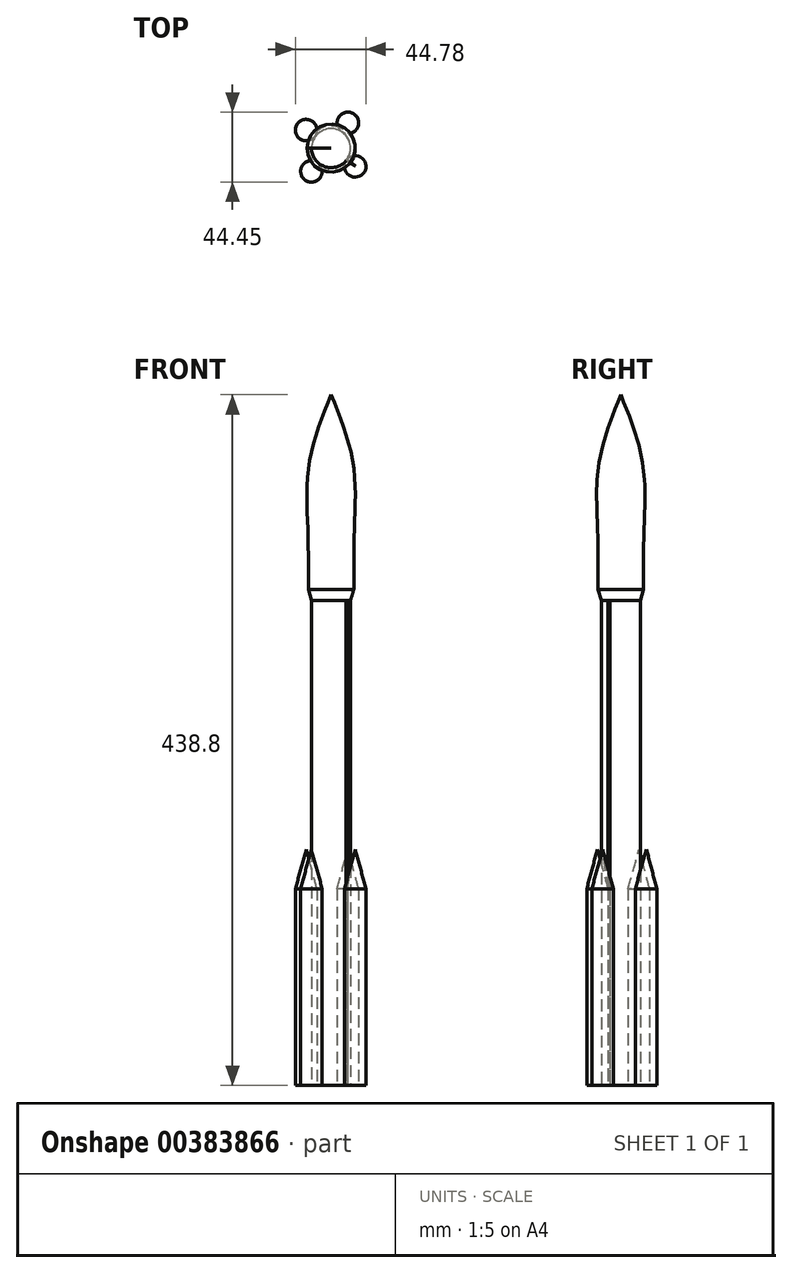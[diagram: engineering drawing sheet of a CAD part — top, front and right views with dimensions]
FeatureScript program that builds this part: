
annotation { "Feature Type Name" : "Feature", "Feature Type Description" : "" }
export const myFeature = defineFeature(function(context is Context, id is Id, definition is map)
    precondition{}
    {
        {
            var Q0;
            Q0=qCreatedBy(makeId("Top.planeOp"),FACE);
            var sketch = newSketch(context, id + "F0", { "sketchPlane" : qUnion([Q0])});
            skCircle(sketch, "E0", {"center": v(0, 0) * mm, "radius": 12.42 * mm});
            skCircle(sketch, "E1", {"center": v(-15.81, 11.43) * mm, "radius": 6.83 * mm});
            skCircle(sketch, "E2", {"center": v(10.7, 16.03) * mm, "radius": 6.83 * mm});
            skCircle(sketch, "E3", {"center": v(-12.48, -14.76) * mm, "radius": 6.83 * mm});
            skCircle(sketch, "E4", {"center": v(15.3, -11.59) * mm, "radius": 6.83 * mm});
            skSolve(sketch);
        }
        {
            var Q0;
            {var subQ0=sQuery(id+"F0.wireOp",EDGE,"E4");var subQ1=sQuery(id+"F0.wireOp",EDGE,"E0");var subQ2=makeQuery(id+"F0.imprint","INTERSECT",VERTEX,{"disambiguationData":[OD(0.0)],"derivedFrom":[subQ1,subQ0]});Q0=makeQuery(id+"F0.imprint","IMPRINT",FACE,{"disambiguationData":[TD([[makeQuery(id+"F0.imprint","IMPRINT",EDGE,{"disambiguationData":[TD([[subQ2,1.0]])],"derivedFrom":subQ1}),1.0]])]});}
            extrude(context, id + "F1", {"entities" : qUnion([Q0]), "depth" : 308 * mm});
        }
        {
            var Q0;
            {var subQ0=sQuery(id+"F0.wireOp",EDGE,"E4");var subQ1=sQuery(id+"F0.wireOp",EDGE,"E0");var subQ2=makeQuery(id+"F0.imprint","INTERSECT",VERTEX,{"disambiguationData":[OD(0.0)],"derivedFrom":[subQ1,subQ0]});Q0=makeQuery(id+"F0.imprint","IMPRINT",FACE,{"disambiguationData":[TD([[makeQuery(id+"F0.imprint","IMPRINT",EDGE,{"disambiguationData":[TD([[subQ2,-1.0]])],"derivedFrom":subQ1}),-1.0]])]});}
            var Q1;
            Q1=makeQuery(id+"F0.imprint","IMPRINT",FACE,{"disambiguationData":[TD([[makeQuery(id+"F0.imprint","IMPRINT",EDGE,{"derivedFrom":sQuery(id+"F0.wireOp",EDGE,"E2")}),1.0]])]});
            var Q2;
            Q2=makeQuery(id+"F0.imprint","IMPRINT",FACE,{"disambiguationData":[TD([[makeQuery(id+"F0.imprint","IMPRINT",EDGE,{"derivedFrom":sQuery(id+"F0.wireOp",EDGE,"E3")}),1.0]])]});
            var Q3;
            Q3=makeQuery(id+"F0.imprint","IMPRINT",FACE,{"disambiguationData":[TD([[makeQuery(id+"F0.imprint","IMPRINT",EDGE,{"derivedFrom":sQuery(id+"F0.wireOp",EDGE,"E1")}),1.0]])]});
            extrude(context, id + "F2", {"entities" : qUnion([Q0, Q1, Q2, Q3]), "depth" : 125 * mm});
        }
        {
            var Q0;
            Q0=makeQuery(id+"F2.opExtrude","CAP_FACE",FACE,{"disambiguationData":[OSD([sQuery(id+"F0.wireOp",EDGE,"E3")])],"isStart":false});
            cPlane(context, id + "F3", {"entities" : qUnion([Q0]), "cplaneType" : CPlaneType.OFFSET, "offset" : 25 * mm, "width" : 150 * mm, "height" : 150 * mm});
        }
        {
            var Q0;
            Q0=qCreatedBy(id+"F3.planeOp",FACE);
            var sketch = newSketch(context, id + "F4", { "sketchPlane" : qUnion([Q0])});
            skCircle(sketch, "E5", {"center": v(-15.72, 11.64) * mm, "radius": 0.7 * mm});
            skCircle(sketch, "E6", {"center": v(-12.58, -14.84) * mm, "radius": 0.65 * mm});
            skCircle(sketch, "E7", {"center": v(15.36, -11.48) * mm, "radius": 0.68 * mm});
            skCircle(sketch, "E8", {"center": v(10.65, 16.24) * mm, "radius": 0.68 * mm});
            skSolve(sketch);
        }
        {
            var Q0;
            Q0=makeQuery(id+"F2.opExtrude","CAP_FACE",FACE,{"disambiguationData":[OSD([sQuery(id+"F0.wireOp",EDGE,"E3")])],"isStart":false});
            var Q1;
            Q1=sQuery(id+"F4.wireOp",VERTEX,"E6.center");
            loft(context, id + "F5", {"sheetProfilesArray" : [{ "sheetProfileEntities" : qUnion([Q0]) }, { "sheetProfileEntities" : qUnion([Q1]) }]});
        }
        {
            var Q1;
            Q1=makeQuery(id+"F2.opExtrude","CAP_FACE",FACE,{"disambiguationData":[OSD([sQuery(id+"F0.wireOp",EDGE,"E0"),sQuery(id+"F0.wireOp",EDGE,"E4")])],"isStart":false});
            var Q2;
            Q2=sQuery(id+"F4.wireOp",VERTEX,"E7.center");
            loft(context, id + "F6", {"operationType" : NewBodyOperationType.ADD, "sheetProfilesArray" : [{ "sheetProfileEntities" : qUnion([Q1]) }, { "sheetProfileEntities" : qUnion([Q2]) }]});
        }
        {
            var Q0;
            Q0=makeQuery(id+"F2.opExtrude","CAP_FACE",FACE,{"disambiguationData":[OSD([sQuery(id+"F0.wireOp",EDGE,"E1")])],"isStart":false});
            var Q1;
            Q1=sQuery(id+"F4.wireOp",VERTEX,"E5.center");
            loft(context, id + "F7", {"sheetProfilesArray" : [{ "sheetProfileEntities" : qUnion([Q0]) }, { "sheetProfileEntities" : qUnion([Q1]) }]});
        }
        {
            var Q0;
            Q0=makeQuery(id+"F2.opExtrude","CAP_FACE",FACE,{"disambiguationData":[OSD([sQuery(id+"F0.wireOp",EDGE,"E2")])],"isStart":false});
            var Q1;
            Q1=sQuery(id+"F4.wireOp",VERTEX,"E8.center");
            loft(context, id + "F8", {"sheetProfilesArray" : [{ "sheetProfileEntities" : qUnion([Q0]) }, { "sheetProfileEntities" : qUnion([Q1]) }]});
        }
        {
            var Q0;
            Q0=makeQuery(id+"F1.opExtrude","CAP_FACE",FACE,{"disambiguationData":[OSD([sQuery(id+"F0.wireOp",EDGE,"E0"),sQuery(id+"F0.wireOp",EDGE,"E4")])],"isStart":false});
            cPlane(context, id + "F9", {"entities" : qUnion([Q0]), "cplaneType" : CPlaneType.OFFSET, "offset" : 7 * mm, "width" : 150 * mm, "height" : 150 * mm});
        }
        {
            var Q0;
            Q0=qCreatedBy(id+"F9.planeOp",FACE);
            var sketch = newSketch(context, id + "F10", { "sketchPlane" : qUnion([Q0])});
            skCircle(sketch, "E9", {"center": v(0, 0) * mm, "radius": 14.45 * mm});
            skSolve(sketch);
        }
        {
            var Q0;
            Q0=makeQuery(id+"F1.opExtrude","CAP_FACE",FACE,{"disambiguationData":[OSD([sQuery(id+"F0.wireOp",EDGE,"E0"),sQuery(id+"F0.wireOp",EDGE,"E4")])],"isStart":false});
            var sketch = newSketch(context, id + "F11", { "sketchPlane" : qUnion([Q0])});
            skCircle(sketch, "E10", {"center": v(0, 0) * mm, "radius": 12.34 * mm});
            skSolve(sketch);
        }
        {
            var Q1;
            Q1=makeQuery(id+"F11.imprint","IMPRINT",FACE,{"disambiguationData":[TD([[makeQuery(id+"F11.imprint","IMPRINT",EDGE,{"derivedFrom":sQuery(id+"F11.wireOp",EDGE,"E10")}),1.0]])]});
            var Q2;
            Q2=makeQuery(id+"F10.imprint","IMPRINT",FACE,{"disambiguationData":[TD([[makeQuery(id+"F10.imprint","IMPRINT",EDGE,{"derivedFrom":sQuery(id+"F10.wireOp",EDGE,"E9")}),1.0]])]});
            loft(context, id + "F12", {"operationType" : NewBodyOperationType.ADD, "sheetProfilesArray" : [{ "sheetProfileEntities" : qUnion([Q1]) }, { "sheetProfileEntities" : qUnion([Q2]) }]});
        }
        {
            var Q0;
            Q0=qCreatedBy(id+"F9.planeOp",FACE);
            cPlane(context, id + "F13", {"entities" : qUnion([Q0]), "cplaneType" : CPlaneType.OFFSET, "offset" : 39.7 * mm, "width" : 150 * mm, "height" : 150 * mm});
        }
        {
            var Q0;
            Q0=qCreatedBy(id+"F13.planeOp",FACE);
            var sketch = newSketch(context, id + "F14", { "sketchPlane" : qUnion([Q0])});
            skCircle(sketch, "E11", {"center": v(0, 0) * mm, "radius": 14.78 * mm});
            skSolve(sketch);
        }
        {
            var Q0;
            Q0=qCreatedBy(id+"F13.planeOp",FACE);
            cPlane(context, id + "F15", {"entities" : qUnion([Q0]), "cplaneType" : CPlaneType.OFFSET, "offset" : 37.1 * mm, "width" : 150 * mm, "height" : 150 * mm});
        }
        {
            var Q0;
            Q0=qCreatedBy(id+"F15.planeOp",FACE);
            var sketch = newSketch(context, id + "F16", { "sketchPlane" : qUnion([Q0])});
            skCircle(sketch, "E12", {"center": v(0, 0) * mm, "radius": 14.46 * mm});
            skSolve(sketch);
        }
        {
            var Q0;
            Q0=qCreatedBy(id+"F15.planeOp",FACE);
            cPlane(context, id + "F17", {"entities" : qUnion([Q0]), "cplaneType" : CPlaneType.OFFSET, "offset" : 47 * mm, "width" : 150 * mm, "height" : 150 * mm});
        }
        {
            var Q0;
            Q0=qCreatedBy(id+"F17.planeOp",FACE);
            var sketch = newSketch(context, id + "F18", { "sketchPlane" : qUnion([Q0])});
            skCircle(sketch, "E13", {"center": v(0, 0) * mm, "radius": 2.54 * mm});
            skSolve(sketch);
        }
        {
            var Q1;
            Q1=makeQuery(id+"F10.imprint","IMPRINT",FACE,{"disambiguationData":[TD([[makeQuery(id+"F10.imprint","IMPRINT",EDGE,{"derivedFrom":sQuery(id+"F10.wireOp",EDGE,"E9")}),1.0]])]});
            var Q2;
            Q2=makeQuery(id+"F14.imprint","IMPRINT",FACE,{"disambiguationData":[TD([[makeQuery(id+"F14.imprint","IMPRINT",EDGE,{"derivedFrom":sQuery(id+"F14.wireOp",EDGE,"E11")}),1.0]])]});
            var Q3;
            Q3=makeQuery(id+"F16.imprint","IMPRINT",FACE,{"disambiguationData":[TD([[makeQuery(id+"F16.imprint","IMPRINT",EDGE,{"derivedFrom":sQuery(id+"F16.wireOp",EDGE,"E12")}),1.0]])]});
            var Q4;
            Q4=sQuery(id+"F18.wireOp",VERTEX,"E13.center");
            loft(context, id + "F19", {"operationType" : NewBodyOperationType.ADD, "sheetProfilesArray" : [{ "sheetProfileEntities" : qUnion([Q1]) }, { "sheetProfileEntities" : qUnion([Q2]) }, { "sheetProfileEntities" : qUnion([Q3]) }, { "sheetProfileEntities" : qUnion([Q4]) }]});
        }
    });
